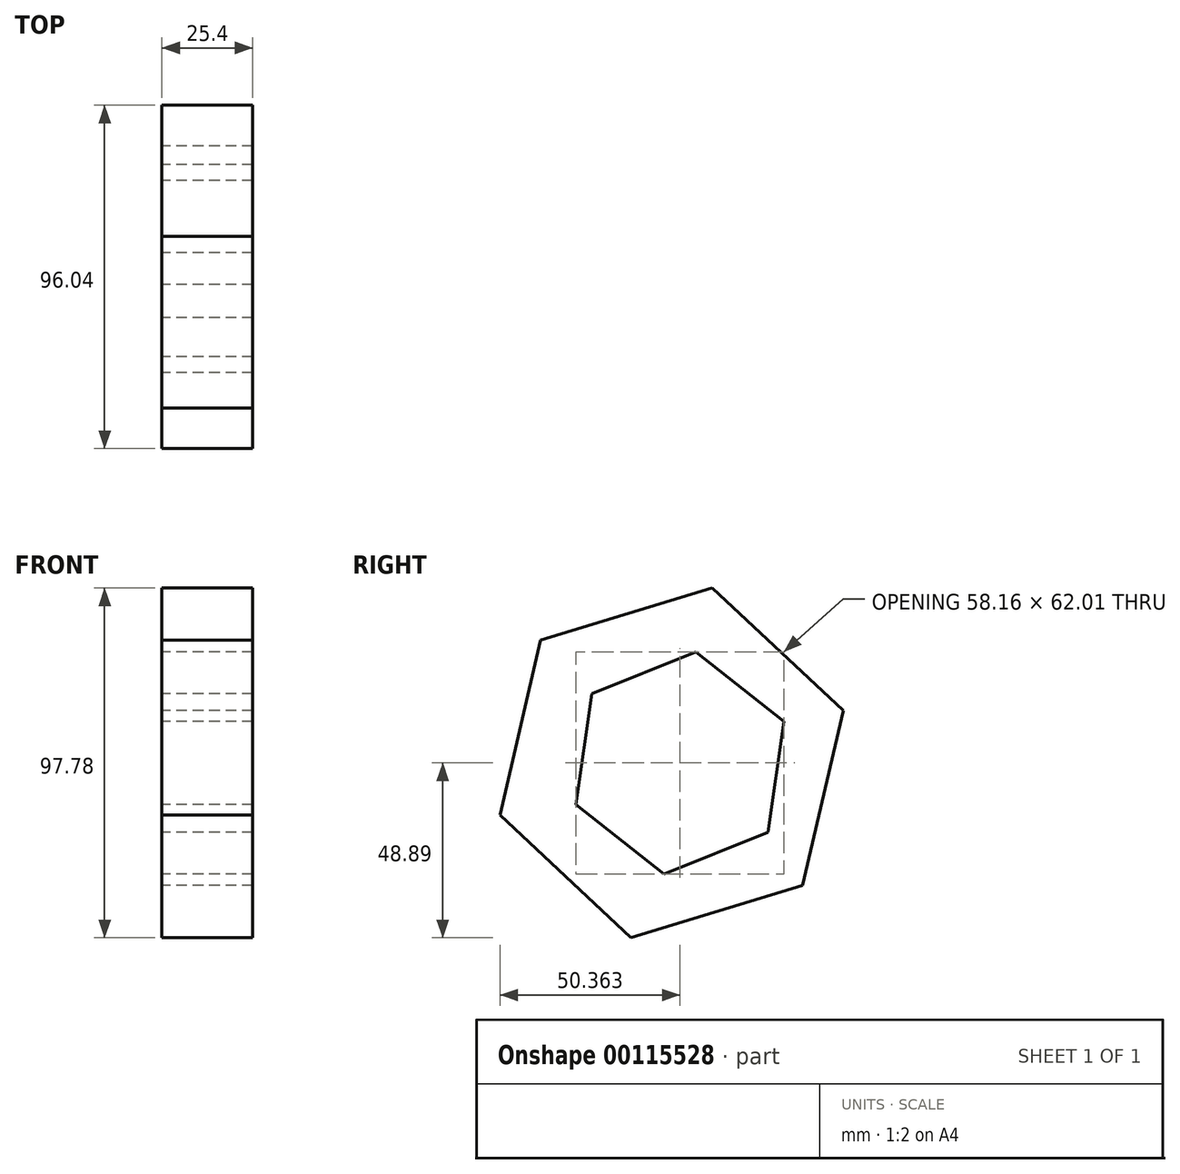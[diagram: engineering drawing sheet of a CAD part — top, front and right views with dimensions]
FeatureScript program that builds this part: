
annotation { "Feature Type Name" : "Feature", "Feature Type Description" : "" }
export const myFeature = defineFeature(function(context is Context, id is Id, definition is map)
    precondition{}
    {
        {
            var Q0;
            Q0=qCreatedBy(makeId("Right.planeOp"),FACE);
            var sketch = newSketch(context, id + "F0", { "sketchPlane" : qUnion([Q0])});
            skCircle(sketch, "E0.cCircle", {"center": v(0, 0) * mm, "radius": 43.47 * mm, "construction": true});
            skLineSegment(sketch, "E0.0", {"start": v(-36.66, 34.28) * mm, "end": v(11.36, 48.9) * mm});
            skLineSegment(sketch, "E0.1", {"start": v(11.36, 48.9) * mm, "end": v(48.02, 14.6) * mm});
            skLineSegment(sketch, "E0.2", {"start": v(48.02, 14.6) * mm, "end": v(36.66, -34.28) * mm});
            skLineSegment(sketch, "E0.3", {"start": v(36.66, -34.28) * mm, "end": v(-11.36, -48.9) * mm});
            skLineSegment(sketch, "E0.4", {"start": v(-11.36, -48.9) * mm, "end": v(-48.02, -14.6) * mm});
            skLineSegment(sketch, "E0.5", {"start": v(-48.02, -14.6) * mm, "end": v(-36.66, 34.28) * mm});
            skPoint(sketch, "E0.0.midPoint", {"position": v(-12.65, 41.59) * mm});
            skCircle(sketch, "E1.cCircle", {"center": v(2.34, 0) * mm, "radius": 27.13 * mm, "construction": true});
            skLineSegment(sketch, "E1.0", {"start": v(-22.27, 19.37) * mm, "end": v(6.8, 31) * mm});
            skLineSegment(sketch, "E1.1", {"start": v(6.8, 31) * mm, "end": v(31.43, 11.63) * mm});
            skLineSegment(sketch, "E1.2", {"start": v(31.43, 11.63) * mm, "end": v(26.96, -19.37) * mm});
            skLineSegment(sketch, "E1.3", {"start": v(26.96, -19.37) * mm, "end": v(-2.12, -31) * mm});
            skLineSegment(sketch, "E1.4", {"start": v(-2.12, -31) * mm, "end": v(-26.74, -11.63) * mm});
            skLineSegment(sketch, "E1.5", {"start": v(-26.74, -11.63) * mm, "end": v(-22.27, 19.37) * mm});
            skPoint(sketch, "E1.0.midPoint", {"position": v(-7.73, 25.19) * mm});
            skLineSegment(sketch, "E2", {"start": v(11.36, 48.9) * mm, "end": v(6.8, 31) * mm});
            skLineSegment(sketch, "E3", {"start": v(48.02, 14.6) * mm, "end": v(31.43, 11.63) * mm});
            skLineSegment(sketch, "E4", {"start": v(36.66, -34.28) * mm, "end": v(26.96, -19.37) * mm});
            skLineSegment(sketch, "E5", {"start": v(-2.12, -31) * mm, "end": v(-11.36, -48.9) * mm});
            skLineSegment(sketch, "E6", {"start": v(-26.74, -11.63) * mm, "end": v(-48.02, -14.6) * mm});
            skLineSegment(sketch, "E7", {"start": v(-22.27, 19.37) * mm, "end": v(-36.66, 34.28) * mm});
            skSolve(sketch);
        }
        {
            var Q0;
            Q0=makeQuery(id+"F0.imprint","IMPRINT",FACE,{"disambiguationData":[TD([[makeQuery(id+"F0.imprint","IMPRINT",EDGE,{"derivedFrom":sQuery(id+"F0.wireOp",EDGE,"E0.5")}),-1.0]])]});
            var Q1;
            Q1=makeQuery(id+"F0.imprint","IMPRINT",FACE,{"disambiguationData":[TD([[makeQuery(id+"F0.imprint","IMPRINT",EDGE,{"derivedFrom":sQuery(id+"F0.wireOp",EDGE,"E0.0")}),-1.0]])]});
            var Q2;
            Q2=makeQuery(id+"F0.imprint","IMPRINT",FACE,{"disambiguationData":[TD([[makeQuery(id+"F0.imprint","IMPRINT",EDGE,{"derivedFrom":sQuery(id+"F0.wireOp",EDGE,"E0.1")}),-1.0]])]});
            var Q3;
            Q3=makeQuery(id+"F0.imprint","IMPRINT",FACE,{"disambiguationData":[TD([[makeQuery(id+"F0.imprint","IMPRINT",EDGE,{"derivedFrom":sQuery(id+"F0.wireOp",EDGE,"E0.2")}),-1.0]])]});
            var Q4;
            Q4=makeQuery(id+"F0.imprint","IMPRINT",FACE,{"disambiguationData":[TD([[makeQuery(id+"F0.imprint","IMPRINT",EDGE,{"derivedFrom":sQuery(id+"F0.wireOp",EDGE,"E0.3")}),-1.0]])]});
            var Q5;
            Q5=makeQuery(id+"F0.imprint","IMPRINT",FACE,{"disambiguationData":[TD([[makeQuery(id+"F0.imprint","IMPRINT",EDGE,{"derivedFrom":sQuery(id+"F0.wireOp",EDGE,"E0.4")}),-1.0]])]});
            extrude(context, id + "F1", {"entities" : qUnion([Q0, Q1, Q2, Q3, Q4, Q5]), "depth" : 25.4 * mm});
        }
    });
